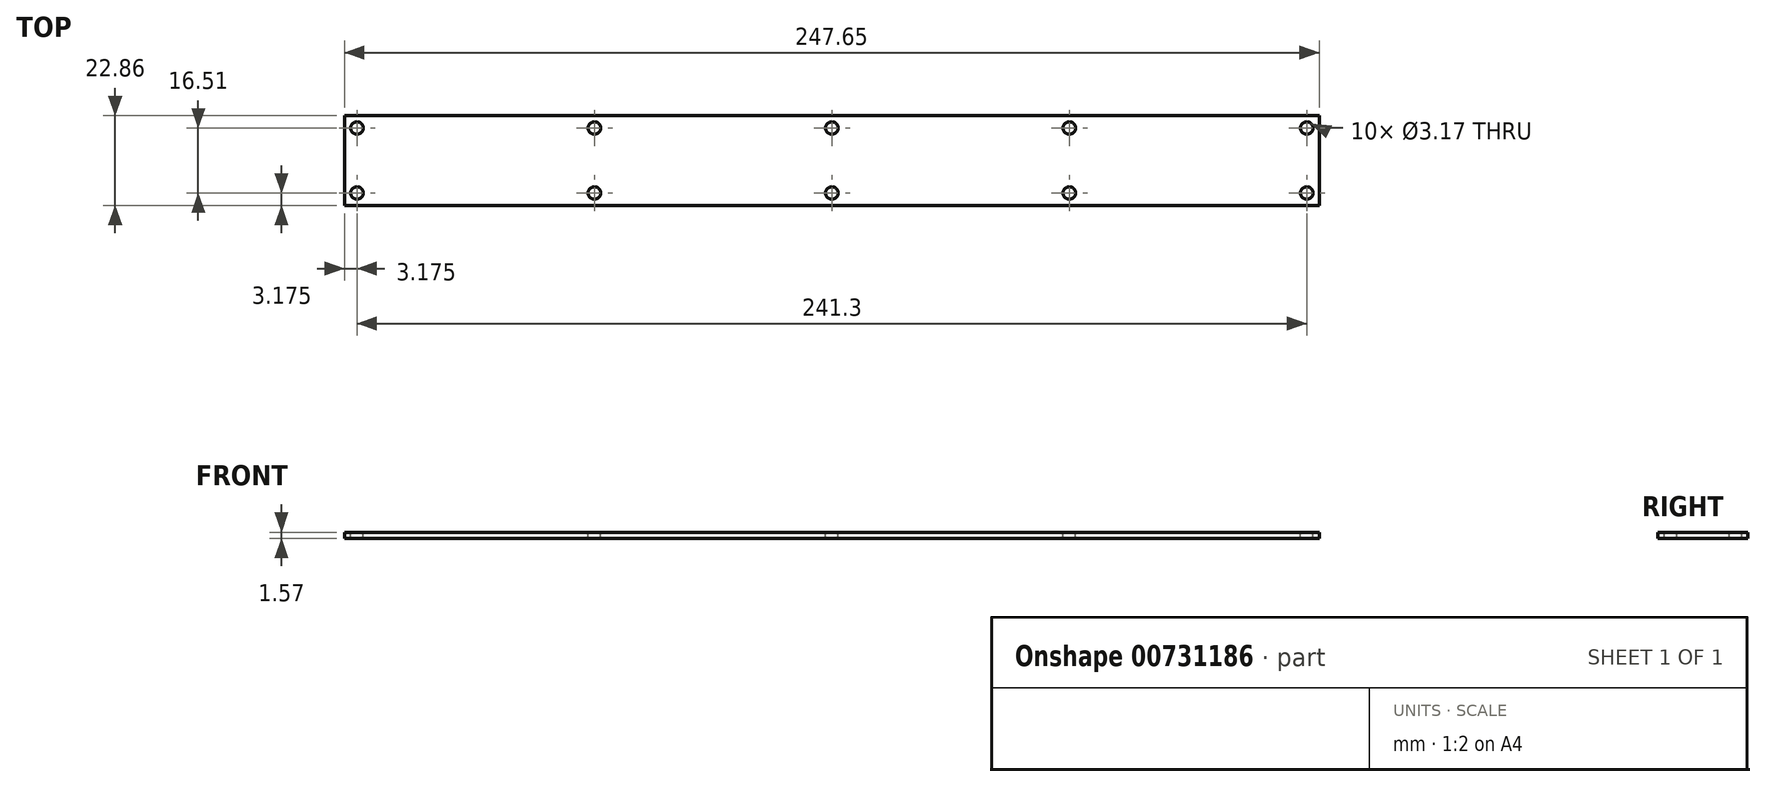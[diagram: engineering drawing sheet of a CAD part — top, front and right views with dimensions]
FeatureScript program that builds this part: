
annotation { "Feature Type Name" : "Feature", "Feature Type Description" : "" }
export const myFeature = defineFeature(function(context is Context, id is Id, definition is map)
    precondition{}
    {
        {
            var Q0;
            Q0=qCreatedBy(makeId("Top.planeOp"),FACE);
            var sketch = newSketch(context, id + "F0", { "sketchPlane" : qUnion([Q0])});
            skLineSegment(sketch, "E0", {"start": v(0, 0) * mm, "end": v(247.65, 0) * mm});
            skLineSegment(sketch, "E1", {"start": v(247.65, 0) * mm, "end": v(247.65, 22.86) * mm});
            skLineSegment(sketch, "E2", {"start": v(247.65, 22.86) * mm, "end": v(0, 22.86) * mm});
            skLineSegment(sketch, "E3", {"start": v(0, 22.86) * mm, "end": v(0, 0) * mm});
            skSolve(sketch);
        }
        {
            var Q0;
            Q0 = qSketchRegion(id + "F0", true);
            extrude(context, id + "F1", {"entities" : qUnion([Q0]), "oppositeDirection" : true, "depth" : 1.57 * mm, "offsetDistance" : 25.4 * mm});
        }
        {
            var Q0;
            Q0=makeQuery(id+"F1.opExtrude","CAP_FACE",FACE,{"disambiguationData":[OSD([sQuery(id+"F0.wireOp",EDGE,"E0"),sQuery(id+"F0.wireOp",EDGE,"E1"),sQuery(id+"F0.wireOp",EDGE,"E2"),sQuery(id+"F0.wireOp",EDGE,"E3")])],"isStart":true});
            var sketch = newSketch(context, id + "F2", { "sketchPlane" : qUnion([Q0])});
            skCircle(sketch, "E4", {"center": v(3.18, 3.18) * mm, "radius": 1.59 * mm});
            skCircle(sketch, "E5", {"center": v(3.17, 19.68) * mm, "radius": 1.59 * mm});
            skCircle(sketch, "E6", {"center": v(244.48, 19.68) * mm, "radius": 1.59 * mm});
            skCircle(sketch, "E7", {"center": v(244.48, 3.17) * mm, "radius": 1.59 * mm});
            skCircle(sketch, "E8", {"center": v(123.83, 3.18) * mm, "radius": 1.59 * mm});
            skCircle(sketch, "E9", {"center": v(123.83, 19.68) * mm, "radius": 1.59 * mm});
            skCircle(sketch, "E10", {"center": v(63.5, 19.69) * mm, "radius": 1.59 * mm});
            skCircle(sketch, "E11", {"center": v(63.5, 3.18) * mm, "radius": 1.59 * mm});
            skCircle(sketch, "E12", {"center": v(184.15, 19.69) * mm, "radius": 1.59 * mm});
            skCircle(sketch, "E13", {"center": v(184.15, 3.18) * mm, "radius": 1.59 * mm});
            skSolve(sketch);
        }
        {
            var Q0;
            Q0 = qSketchRegion(id + "F2", true);
            extrude(context, id + "F3", {"entities" : qUnion([Q0]), "operationType" : NewBodyOperationType.REMOVE, "oppositeDirection" : true, "depth" : 1.57 * mm, "offsetDistance" : 25.4 * mm});
        }
    });
